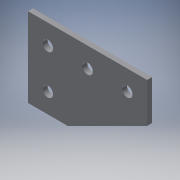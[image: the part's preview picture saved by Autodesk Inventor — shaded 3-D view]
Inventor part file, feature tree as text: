
AUTODESK INVENTOR PART (.ipt)
format: ipt  version: 2016 (Build 200138000, 138)  size: 104,448 bytes
history: native  units: in
note: dims shown in document units (in); Inventor stores cm internally (conversion verified against a paired STEP export)
features: extrude x1, sketch x1
ambient origin geometry x8: Origin, YZ Plane, XZ Plane, XY Plane, X Axis, Y Axis, Z Axis, Center Point
bodies: Solid1 (feature_tree)
feature tree (2):
  extrude  "Extrusion1"  Depth=0.125in
  sketch  "Sketch1"  dims[d0=1.0in d1=1.0in d2=3.0in d3=2.0in d4=0.2656in d5=0.5in d6=0.5in d7=0.5in d8=0.5in d9=0.5in d10=1.5in d11=0.5in d12=0.5in d13=0.125in d14=0.0in]
